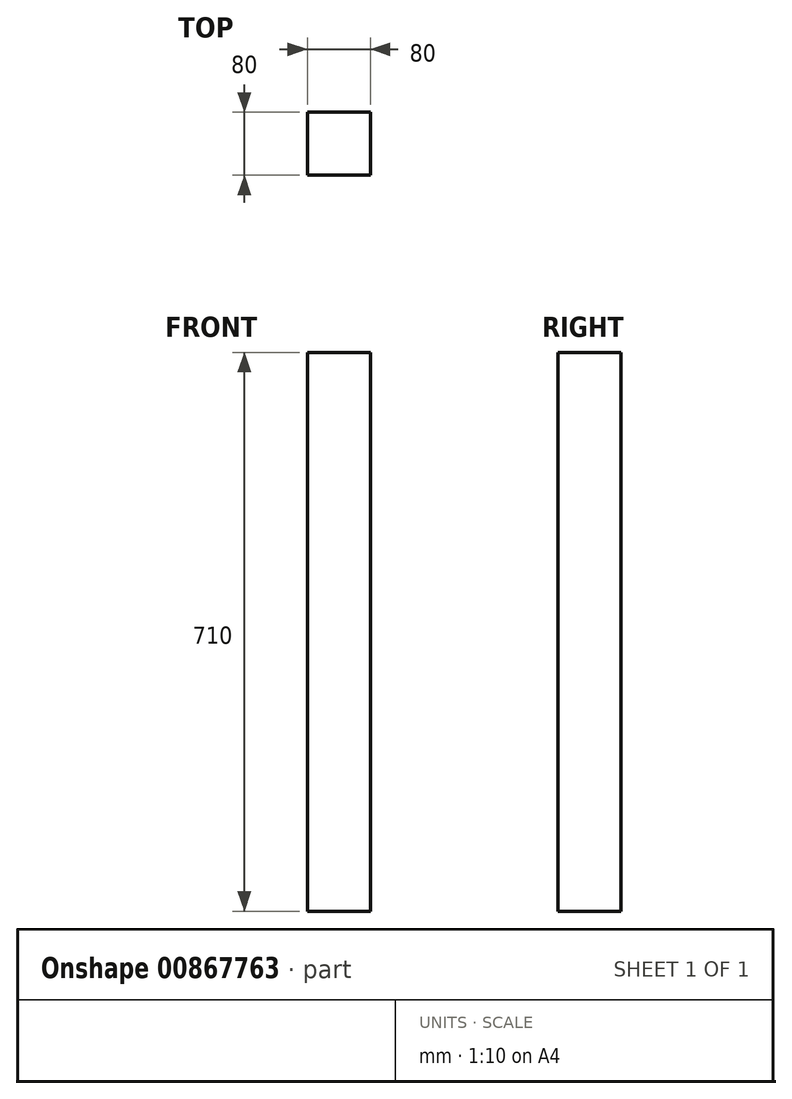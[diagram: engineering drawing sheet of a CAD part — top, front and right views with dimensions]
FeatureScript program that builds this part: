
annotation { "Feature Type Name" : "Feature", "Feature Type Description" : "" }
export const myFeature = defineFeature(function(context is Context, id is Id, definition is map)
    precondition{}
    {
        {
            var Q0;
            Q0=qCreatedBy(makeId("Top.planeOp"),FACE);
            var sketch = newSketch(context, id + "F0", { "sketchPlane" : qUnion([Q0])});
            skLineSegment(sketch, "E0.bottom", {"start": v(40, -40) * mm, "end": v(-40, -40) * mm});
            skLineSegment(sketch, "E0.top", {"start": v(40, 40) * mm, "end": v(-40, 40) * mm});
            skLineSegment(sketch, "E0.left", {"start": v(40, -40) * mm, "end": v(40, 40) * mm});
            skLineSegment(sketch, "E0.right", {"start": v(-40, -40) * mm, "end": v(-40, 40) * mm});
            skPoint(sketch, "E0.middle", {"position": v(0, 0) * mm});
            skSolve(sketch);
        }
        {
            var Q0;
            Q0=makeQuery(id+"F0.imprint","IMPRINT",FACE,{"disambiguationData":[TD([[makeQuery(id+"F0.imprint","IMPRINT",EDGE,{"derivedFrom":sQuery(id+"F0.wireOp",EDGE,"E0.bottom")}),-1.0]])]});
            extrude(context, id + "F1", {"entities" : qUnion([Q0]), "depth" : 710 * mm, "offsetDistance" : 25 * mm});
        }
    });
